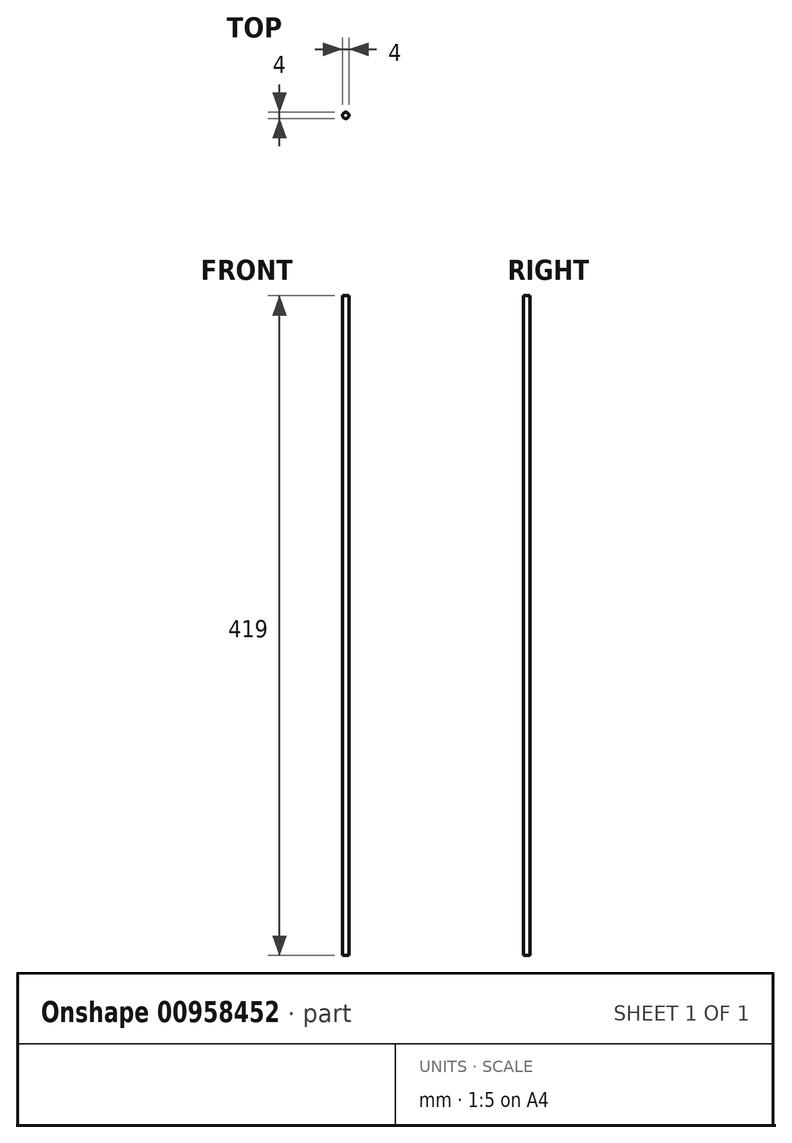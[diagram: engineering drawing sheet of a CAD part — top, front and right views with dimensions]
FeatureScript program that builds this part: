
annotation { "Feature Type Name" : "Feature", "Feature Type Description" : "" }
export const myFeature = defineFeature(function(context is Context, id is Id, definition is map)
    precondition{}
    {
        {
            var Q0;
            Q0=qCreatedBy(makeId("Top.planeOp"),FACE);
            var sketch = newSketch(context, id + "F0", { "sketchPlane" : qUnion([Q0])});
            skCircle(sketch, "E0", {"center": v(0, 0) * mm, "radius": 2 * mm});
            skSolve(sketch);
        }
        {
            var Q0;
            Q0=makeQuery(id+"F0.imprint","IMPRINT",FACE,{"disambiguationData":[TD([[makeQuery(id+"F0.imprint","IMPRINT",EDGE,{"derivedFrom":sQuery(id+"F0.wireOp",EDGE,"E0")}),1.0]])]});
            extrude(context, id + "F1", {"entities" : qUnion([Q0]), "depth" : 419 * mm, "offsetDistance" : 25 * mm});
        }
    });
